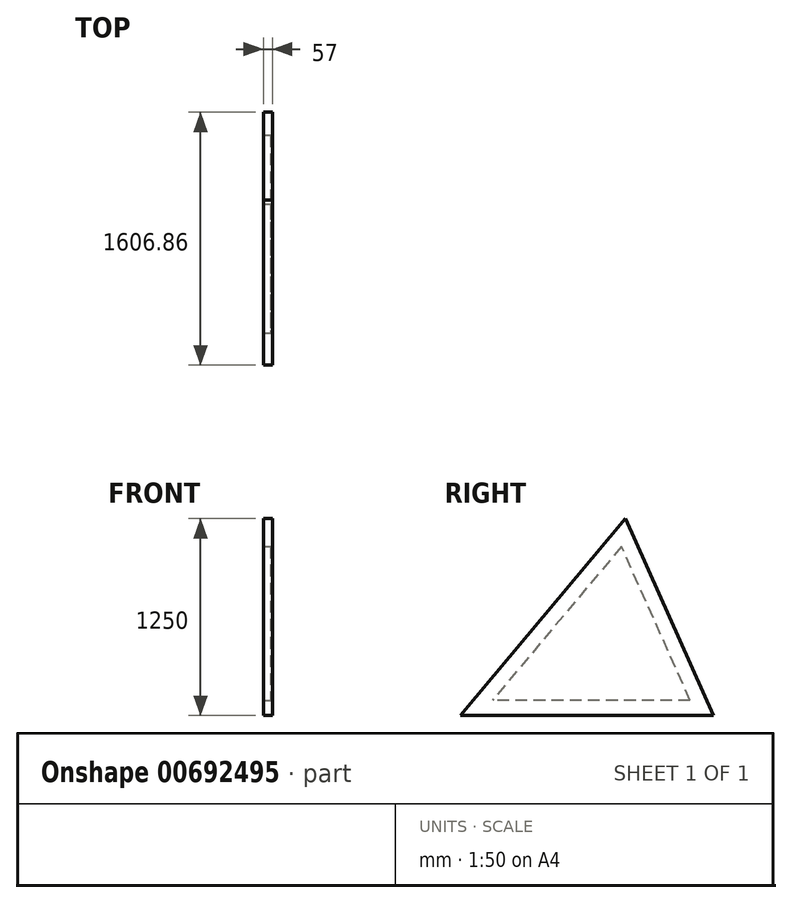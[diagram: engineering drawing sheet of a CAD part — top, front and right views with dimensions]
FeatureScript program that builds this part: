
annotation { "Feature Type Name" : "Feature", "Feature Type Description" : "" }
export const myFeature = defineFeature(function(context is Context, id is Id, definition is map)
    precondition{}
    {
        {
            var Q0;
            Q0=qCreatedBy(makeId("Right.planeOp"),FACE);
            var sketch = newSketch(context, id + "F0", { "sketchPlane" : qUnion([Q0])});
            skPoint(sketch, "E0.MirrorP", {"position": v(1107.56, 1620.74) * mm});
            skPoint(sketch, "E1.MirrorP", {"position": v(207.65, 548.14) * mm});
            skPoint(sketch, "E2.MirrorP", {"position": v(287.35, 643.14) * mm});
            skPoint(sketch, "E3.MirrorP", {"position": v(1586.46, 548.14) * mm});
            skLineSegment(sketch, "E4.MirrorCS", {"start": v(1544.04, 643.14) * mm, "end": v(287.35, 643.14) * mm});
            skLineSegment(sketch, "E5.MirrorCS", {"start": v(1107.56, 1620.74) * mm, "end": v(207.65, 548.14) * mm});
            skPoint(sketch, "E6.MirrorP", {"position": v(1132.4, 1798.14) * mm});
            skLineSegment(sketch, "E7.MirrorCS", {"start": v(1544.04, 643.14) * mm, "end": v(1586.46, 548.14) * mm});
            skLineSegment(sketch, "E8.MirrorCS", {"start": v(1690.5, 548.14) * mm, "end": v(83.64, 548.14) * mm});
            skLineSegment(sketch, "E9.MirrorCS", {"start": v(83.64, 548.14) * mm, "end": v(1132.4, 1798.14) * mm});
            skPoint(sketch, "E10.MirrorP", {"position": v(1690.5, 548.14) * mm});
            skLineSegment(sketch, "E11.MirrorCS", {"start": v(1690.5, 548.14) * mm, "end": v(1132.4, 1798.14) * mm});
            skLineSegment(sketch, "E12.MirrorCS", {"start": v(1544.04, 643.14) * mm, "end": v(1064.49, 1717.2) * mm});
            skPoint(sketch, "E13.MirrorP", {"position": v(1544.04, 643.14) * mm});
            skPoint(sketch, "E14.MirrorP", {"position": v(1064.49, 1717.2) * mm});
            skSolve(sketch);
        }
        {
            var Q0;
            {var subQ2=sQuery(id+"F0.wireOp",EDGE,"E7.MirrorCS");Q0=makeQuery(id+"F0.imprint","IMPRINT",FACE,{"disambiguationData":[TD([[makeQuery(id+"F0.imprint","IMPRINT",EDGE,{"derivedFrom":subQ2}),1.0]])]});}
            var Q1;
            {var subQ2=sQuery(id+"F0.wireOp",EDGE,"E8.MirrorCS");var subQ4=sQuery(id+"F0.wireOp",EDGE,"E9.MirrorCS");var subQ5=makeQuery(id+"F0.imprint","INTERSECT",VERTEX,{"derivedFrom":[subQ2,subQ4]});Q1=makeQuery(id+"F0.imprint","IMPRINT",FACE,{"disambiguationData":[TD([[makeQuery(id+"F0.imprint","IMPRINT",EDGE,{"disambiguationData":[TD([[subQ5,1.0]])],"derivedFrom":subQ2}),-1.0]])]});}
            var Q2;
            {var subQ0=sQuery(id+"F0.wireOp",EDGE,"E7.MirrorCS");Q2=makeQuery(id+"F0.imprint","IMPRINT",FACE,{"disambiguationData":[TD([[makeQuery(id+"F0.imprint","IMPRINT",EDGE,{"derivedFrom":subQ0}),-1.0]])]});}
            extrude(context, id + "F1", {"entities" : qUnion([Q0, Q1, Q2]), "depth" : -57 * mm, "offsetDistance" : 25.4 * mm});
        }
        {
            var Q0;
            {var subQ0=sQuery(id+"F0.wireOp",EDGE,"E4.MirrorCS");Q0=makeQuery(id+"F0.imprint","IMPRINT",FACE,{"disambiguationData":[TD([[makeQuery(id+"F0.imprint","IMPRINT",EDGE,{"derivedFrom":subQ0}),-1.0]])]});}
            extrude(context, id + "F2", {"entities" : qUnion([Q0]), "operationType" : NewBodyOperationType.ADD, "depth" : -12 * mm, "offsetDistance" : 25.4 * mm});
        }
    });
